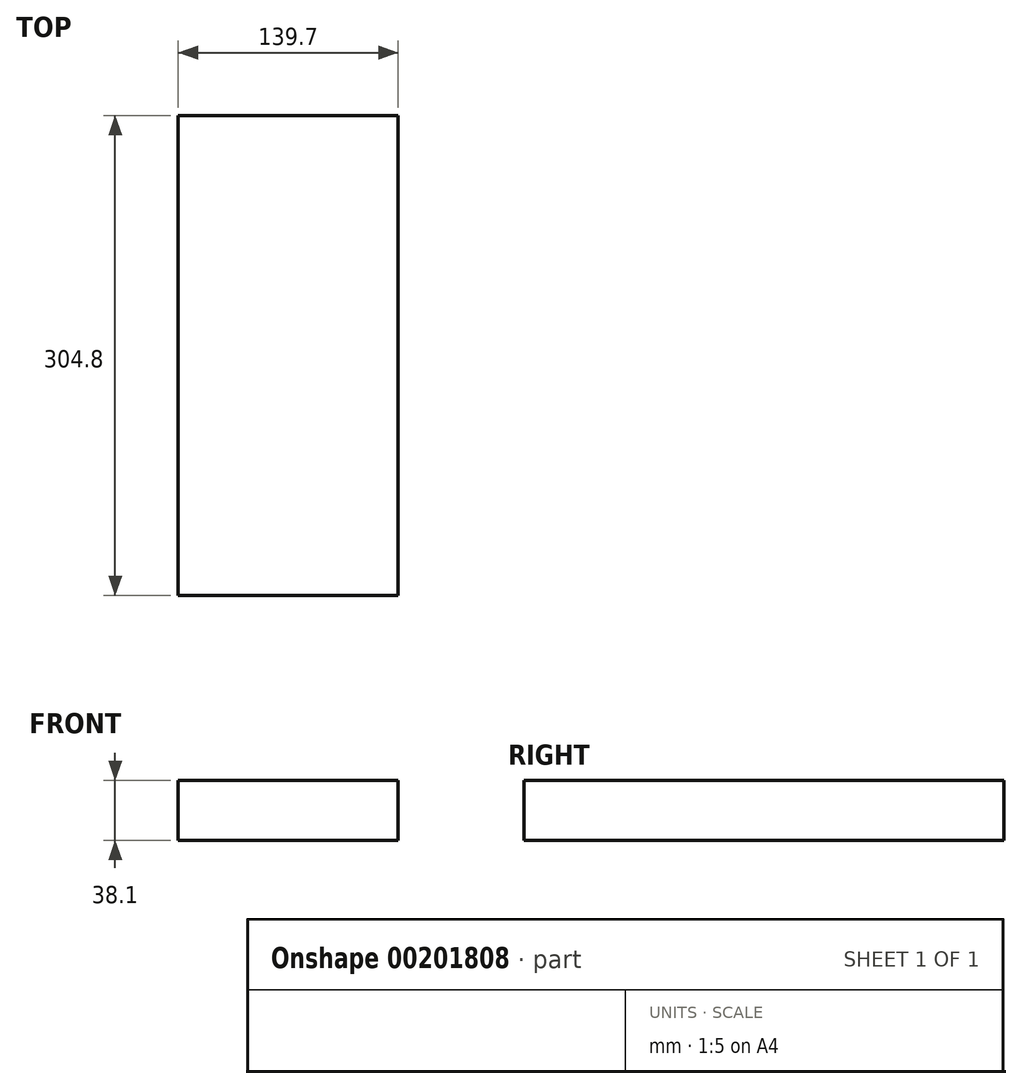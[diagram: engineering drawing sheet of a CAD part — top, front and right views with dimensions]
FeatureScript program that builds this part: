
annotation { "Feature Type Name" : "Feature", "Feature Type Description" : "" }
export const myFeature = defineFeature(function(context is Context, id is Id, definition is map)
    precondition{}
    {
        {
            var Q0;
            Q0=qCreatedBy(makeId("Front.planeOp"),FACE);
            var sketch = newSketch(context, id + "F0", { "sketchPlane" : qUnion([Q0])});
            skLineSegment(sketch, "E0.bottom", {"start": v(69.85, -19.05) * mm, "end": v(-69.85, -19.05) * mm});
            skLineSegment(sketch, "E0.top", {"start": v(69.85, 19.05) * mm, "end": v(-69.85, 19.05) * mm});
            skLineSegment(sketch, "E0.left", {"start": v(69.85, -19.05) * mm, "end": v(69.85, 19.05) * mm});
            skLineSegment(sketch, "E0.right", {"start": v(-69.85, -19.05) * mm, "end": v(-69.85, 19.05) * mm});
            skPoint(sketch, "E0.middle", {"position": v(0, 0) * mm});
            skSolve(sketch);
        }
        {
            var Q0;
            Q0 = qSketchRegion(id + "F0", true);
            extrude(context, id + "F1", {"entities" : qUnion([Q0]), "depth" : 304.8 * mm});
        }
    });
